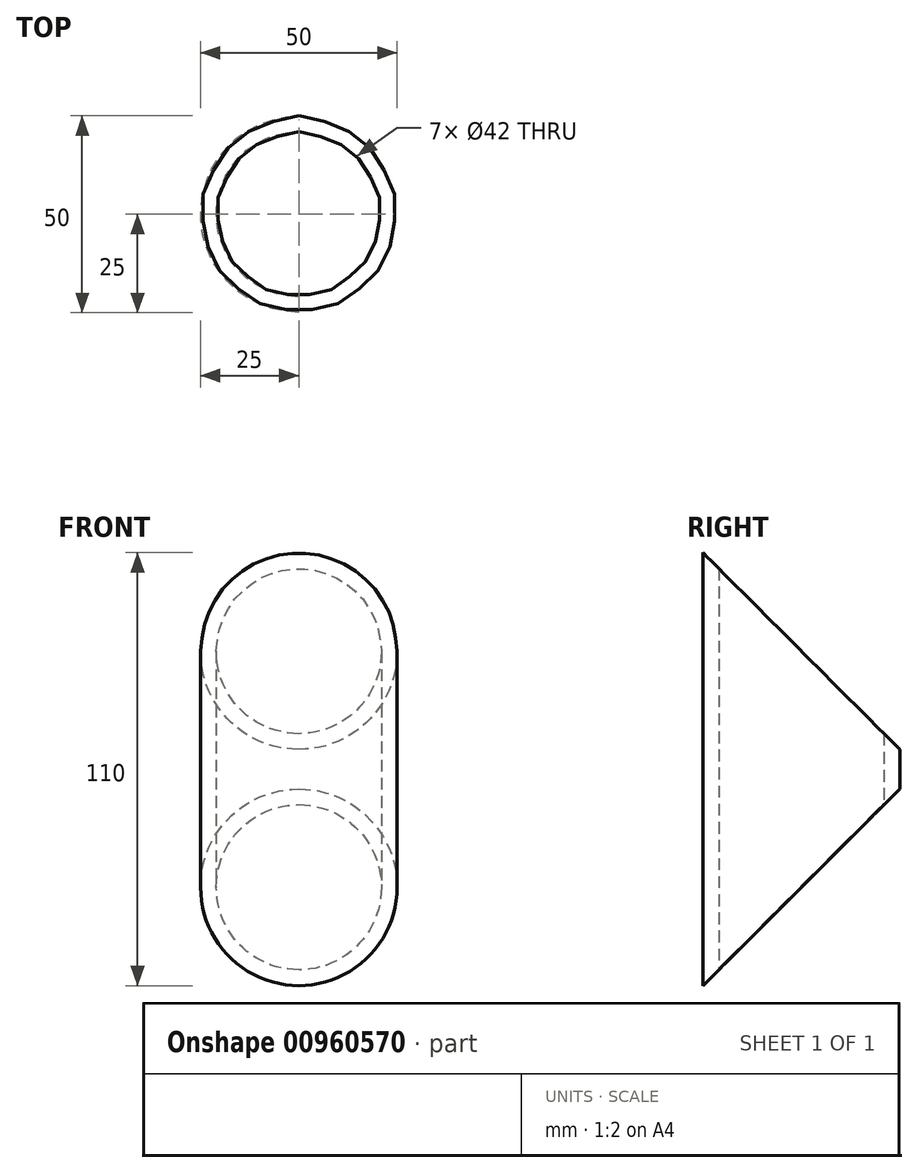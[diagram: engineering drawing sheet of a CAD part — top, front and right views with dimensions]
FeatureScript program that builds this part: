
annotation { "Feature Type Name" : "Feature", "Feature Type Description" : "" }
export const myFeature = defineFeature(function(context is Context, id is Id, definition is map)
    precondition{}
    {
        {
            var Q0;
            Q0=qCreatedBy(makeId("Right.planeOp"),FACE);
            var sketch = newSketch(context, id + "F0", { "sketchPlane" : qUnion([Q0])});
            skLineSegment(sketch, "E0", {"start": v(0, 0) * mm, "end": v(-50, 0) * mm});
            skLineSegment(sketch, "E1", {"start": v(-50, 0) * mm, "end": v(-50, 71.76) * mm});
            skLineSegment(sketch, "E2", {"start": v(-50, 71.76) * mm, "end": v(0, 71.76) * mm});
            skLineSegment(sketch, "E3", {"start": v(0, 50) * mm, "end": v(0, 0) * mm});
            skLineSegment(sketch, "E4", {"start": v(-50, 0) * mm, "end": v(0, 50) * mm});
            skLineSegment(sketch, "E5", {"start": v(0, 50) * mm, "end": v(0, 60) * mm});
            skLineSegment(sketch, "E6", {"start": v(0, 60) * mm, "end": v(-50, 110) * mm});
            skLineSegment(sketch, "E7", {"start": v(-50, 110) * mm, "end": v(-50, 71.76) * mm});
            skLineSegment(sketch, "E8", {"start": v(-50, 110) * mm, "end": v(0, 110) * mm});
            skLineSegment(sketch, "E9", {"start": v(0, 110) * mm, "end": v(0, 60) * mm});
            skSolve(sketch);
        }
        {
            var Q0;
            Q0=qCreatedBy(makeId("Top.planeOp"),FACE);
            var sketch = newSketch(context, id + "F1", { "sketchPlane" : qUnion([Q0])});
            skLineSegment(sketch, "E10", {"start": v(0, 0) * mm, "end": v(0, -25) * mm});
            skCircle(sketch, "E11", {"center": v(0, -25) * mm, "radius": 21 * mm});
            skCircle(sketch, "E12", {"center": v(0, -25) * mm, "radius": 25 * mm});
            skSolve(sketch);
        }
        {
            var Q0;
            Q0 = qSketchRegion(id + "F1", true);
            extrude(context, id + "F2", {"entities" : qUnion([Q0]), "depth" : 110 * mm, "offsetDistance" : 25 * mm});
        }
        {
            var Q0;
            Q0=makeQuery(id+"F0.imprint","IMPRINT",FACE,{"disambiguationData":[TD([[makeQuery(id+"F0.imprint","IMPRINT",EDGE,{"derivedFrom":sQuery(id+"F0.wireOp",EDGE,"E0")}),-1.0]])]});
            var Q1;
            {var subQ0=sQuery(id+"F0.wireOp",EDGE,"E9");var subQ1=sQuery(id+"F0.wireOp",EDGE,"E2");var subQ2=makeQuery(id+"F0.imprint","INTERSECT",VERTEX,{"derivedFrom":[subQ1,subQ0]});Q1=makeQuery(id+"F0.imprint","IMPRINT",FACE,{"disambiguationData":[TD([[makeQuery(id+"F0.imprint","IMPRINT",EDGE,{"disambiguationData":[TD([[subQ2,1.0]])],"derivedFrom":subQ1}),-1.0]])]});}
            var Q2;
            {var subQ5=sQuery(id+"F0.wireOp",EDGE,"E8");Q2=makeQuery(id+"F0.imprint","IMPRINT",FACE,{"disambiguationData":[TD([[makeQuery(id+"F0.imprint","IMPRINT",EDGE,{"derivedFrom":subQ5}),-1.0]])]});}
            extrude(context, id + "F3", {"entities" : qUnion([Q0, Q1, Q2]), "operationType" : NewBodyOperationType.REMOVE, "oppositeDirection" : true, "depth" : 50 * mm, "offsetDistance" : 25 * mm, "symmetric" : true});
        }
    });
